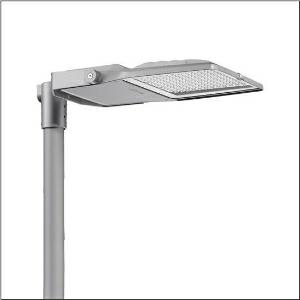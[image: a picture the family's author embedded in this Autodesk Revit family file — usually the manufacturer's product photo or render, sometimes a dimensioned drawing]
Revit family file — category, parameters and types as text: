
# Revit family: floodlight_fl_21_iq_midi___pl33t_5xa7782e4f3a_344b
name_source: partatom
category: Lighting Fixtures
units: mm (PartAtom-declared; Revit-internal decimal feet)

## family parameters
Cut with Voids When Loaded = No
Host = Face
Light Source = No
Part Type = Normal
Room Calculation Point = No
Round Connector Dimension = Use Diameter
Shared = No

## types (1)
- --- (1 x LED, 27690 lm, 208.1 W, 4000K)
    Apparent Load = 208 VA
    CIE Flux Codes = 26 75 99 100 100
    Color Rendering = 70
    Color Temperature = 4000K
    Default Elevation = 1800 mm
    Description = Floodlight FL 21 iQ midi, floodlight, primary light control with lens, of PMMA, primary optical cover: protective disc, of toughened safety glass, transparent, light distribution: PL33T, light emission: direct distribution, installation type: surface-mounted, LED, High Power LED, rated luminous flux: 27.690lm, luminous efficacy: 133lm/W, light colour: 740, colour temperature: 4000K, control gear: iQ Street-Remote/DALI, control: optimised constant luminous flux control (CLO 2.0), Desk-Remote (wireless, voltage-free reading and setting of iQ features in the workshop via application-optimized NFC function/RFID function), Smart-Wire, Night-Set, Temp-Guard, Auto-Match, Street-Remote, with terminal, 6-pole, mains connection: 220..240V, AC, 50/60Hz, start of lifetime: 208W, end of service life: 227W, reduction: 90W, luminaire housing, of diecast aluminium, powder-coated, Siteco® metallic grey (DB 702S), corrosivity category C5 mid according to DIN EN ISO 12944, suitable for swimming pools, chlorine-resistant, sealing non-destructively replaceable, please order mast flange separately, mast bracket, of steel, galvanised, powder-coated, Siteco® metallic grey (DB 702S), protection rating (complete): IP66, insulation class (complete): insulation class II (safety insulation), certification: CE, ENEC, VDE, protection symbol: D, impact resistance: IK08, permissible operating ambient temperature: -40..+40°C, permissible operating ambient temperature for outdoor applications: -40..+50°C, standard: DIN EN 12944, LABS conformity tested according to VDMA 24364:2018-05, packaging unit: 1 piece

Light Distribution: PL33T
    Height = 76 mm
    Lamp = 1 x LED
    Lamp Light Flux = 27690 lm
    Lamp Power = 208.1 W
    Lamp count = 1
    Length = 657 mm
    Luminous efficacy = 133 lm/W
    Manufacturer = Siteco
    ModVariant = No
    Model = 5XA7782E4F3A
    Number of Poles = 1
    OnlyDefault = Yes
    Power Factor = 1
    Product Name = Floodlight FL 21 iQ midi | PL33T
    Product group = floodlight | pylon annexe
    ProductGroupID = 6201
    Protection Class = Protection class II
    Protection Degree = IP 66
    RLX_Detail_Level = 1
    RLX_Emergency_Light_Flux = 0 lm
    RLX_Emergency_Type = 0
    RLX_Emergency_Type_DB = No
    RlxData = <blob elided: 153609 chars, md5=88cc7feb>
    Socket = socket
    Standby Power = 0 W
    System Light Flux = 27690 lm
    System Power = 208 W
    Type Comments = factory setting: luminous flux: 100 % | dim-lin: 254 | 710 mA
    Type Image = l_1007123.jpg
    URL = http://relux.com
    VarID = @adj_125149
    Voltage = 0 V
    Weight = 0.00 kg
    Width = 442 mm

## geometry (parser evidence)
native form markers: Blend x4, Sweep x12
no freeform markers — native parametric forms only
